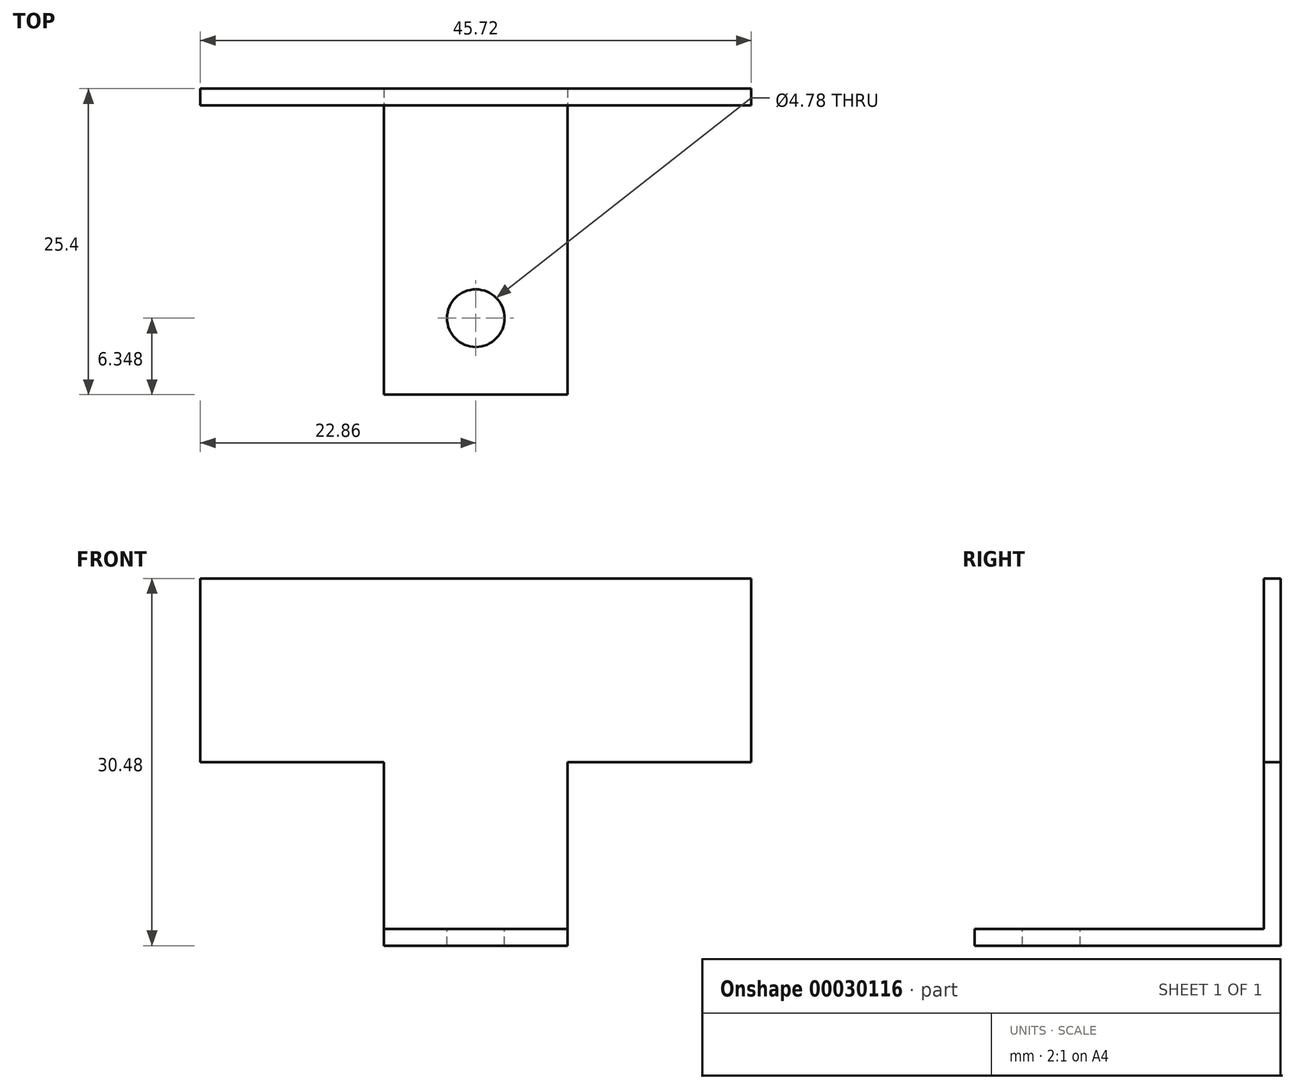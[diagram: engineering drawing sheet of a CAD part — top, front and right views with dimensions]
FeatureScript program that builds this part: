
annotation { "Feature Type Name" : "Feature", "Feature Type Description" : "" }
export const myFeature = defineFeature(function(context is Context, id is Id, definition is map)
    precondition{}
    {
        {
            var Q0;
            Q0=qCreatedBy(makeId("Front.planeOp"),FACE);
            var sketch = newSketch(context, id + "F0", { "sketchPlane" : qUnion([Q0])});
            skLineSegment(sketch, "E0.bottom", {"start": v(-22.86, -15.24) * mm, "end": v(22.86, -15.24) * mm});
            skLineSegment(sketch, "E0.top", {"start": v(-22.86, 15.24) * mm, "end": v(22.86, 15.24) * mm});
            skLineSegment(sketch, "E0.left", {"start": v(-22.86, -15.24) * mm, "end": v(-22.86, 15.24) * mm});
            skLineSegment(sketch, "E0.right", {"start": v(22.86, -15.24) * mm, "end": v(22.86, 15.24) * mm});
            skSolve(sketch);
        }
        {
            var Q0;
            Q0=qSketchRegion(id+"F0",true);
            extrude(context, id + "F1", {"entities" : qUnion([Q0]), "endBound" : BoundingType.SYMMETRIC, "depth" : 1.4 * mm});
        }
        {
            var Q0;
            Q0=makeQuery(id+"F1.opExtrude","CAP_FACE",FACE,{"disambiguationData":[OSD([sQuery(id+"F0.wireOp",EDGE,"E0.bottom"),sQuery(id+"F0.wireOp",EDGE,"E0.top"),sQuery(id+"F0.wireOp",EDGE,"E0.left"),sQuery(id+"F0.wireOp",EDGE,"E0.right")])],"isStart":false});
            var sketch = newSketch(context, id + "F2", { "sketchPlane" : qUnion([Q0])});
            skLineSegment(sketch, "E1.bottom", {"start": v(-22.86, -15.24) * mm, "end": v(-7.62, -15.24) * mm});
            skLineSegment(sketch, "E1.top", {"start": v(-22.86, 0) * mm, "end": v(-7.62, 0) * mm});
            skLineSegment(sketch, "E1.left", {"start": v(-22.86, -15.24) * mm, "end": v(-22.86, 0) * mm});
            skLineSegment(sketch, "E1.right", {"start": v(-7.62, -15.24) * mm, "end": v(-7.62, 0) * mm});
            skLineSegment(sketch, "E2.MirrorCS", {"start": v(7.62, -15.24) * mm, "end": v(7.62, 0) * mm});
            skLineSegment(sketch, "E3.MirrorCS", {"start": v(22.86, 0) * mm, "end": v(7.62, 0) * mm});
            skLineSegment(sketch, "E4.MirrorCS", {"start": v(22.86, -15.24) * mm, "end": v(22.86, 0) * mm});
            skLineSegment(sketch, "E5.MirrorCS", {"start": v(22.86, -15.24) * mm, "end": v(7.62, -15.24) * mm});
            skSolve(sketch);
        }
        {
            var Q0;
            Q0=qSketchRegion(id+"F2",true);
            extrude(context, id + "F3", {"entities" : qUnion([Q0]), "operationType" : NewBodyOperationType.REMOVE, "endBound" : BoundingType.THROUGH_ALL, "oppositeDirection" : true, "depth" : 25.4 * mm});
        }
        {
            var Q0;
            Q0=makeQuery(id+"F1.opExtrude","CAP_FACE",FACE,{"disambiguationData":[OSD([sQuery(id+"F0.wireOp",EDGE,"E0.bottom"),sQuery(id+"F0.wireOp",EDGE,"E0.top"),sQuery(id+"F0.wireOp",EDGE,"E0.left"),sQuery(id+"F0.wireOp",EDGE,"E0.right")])],"isStart":false});
            var sketch = newSketch(context, id + "F4", { "sketchPlane" : qUnion([Q0])});
            skLineSegment(sketch, "E6.bottom", {"start": v(-7.62, -15.24) * mm, "end": v(7.62, -15.24) * mm});
            skLineSegment(sketch, "E6.top", {"start": v(-7.62, -13.84) * mm, "end": v(7.62, -13.84) * mm});
            skLineSegment(sketch, "E6.left", {"start": v(-7.62, -15.24) * mm, "end": v(-7.62, -13.84) * mm});
            skLineSegment(sketch, "E6.right", {"start": v(7.62, -15.24) * mm, "end": v(7.62, -13.84) * mm});
            skSolve(sketch);
        }
        {
            var Q0;
            Q0=qSketchRegion(id+"F4",true);
            extrude(context, id + "F5", {"entities" : qUnion([Q0]), "operationType" : NewBodyOperationType.ADD, "depth" : 24 * mm});
        }
        {
            var Q0;
            Q0=makeQuery(id+"F5.opExtrude","SWEPT_FACE",FACE,{"disambiguationData":[OSD([sQuery(id+"F4.wireOp",EDGE,"E6.top")])]});
            var sketch = newSketch(context, id + "F6", { "sketchPlane" : qUnion([Q0])});
            skCircle(sketch, "E7", {"center": v(0, -18.35) * mm, "radius": 2.39 * mm});
            skSolve(sketch);
        }
        {
            var Q0;
            Q0=qSketchRegion(id+"F6",true);
            extrude(context, id + "F7", {"entities" : qUnion([Q0]), "operationType" : NewBodyOperationType.REMOVE, "endBound" : BoundingType.THROUGH_ALL, "oppositeDirection" : true, "depth" : 25.4 * mm});
        }
    });
